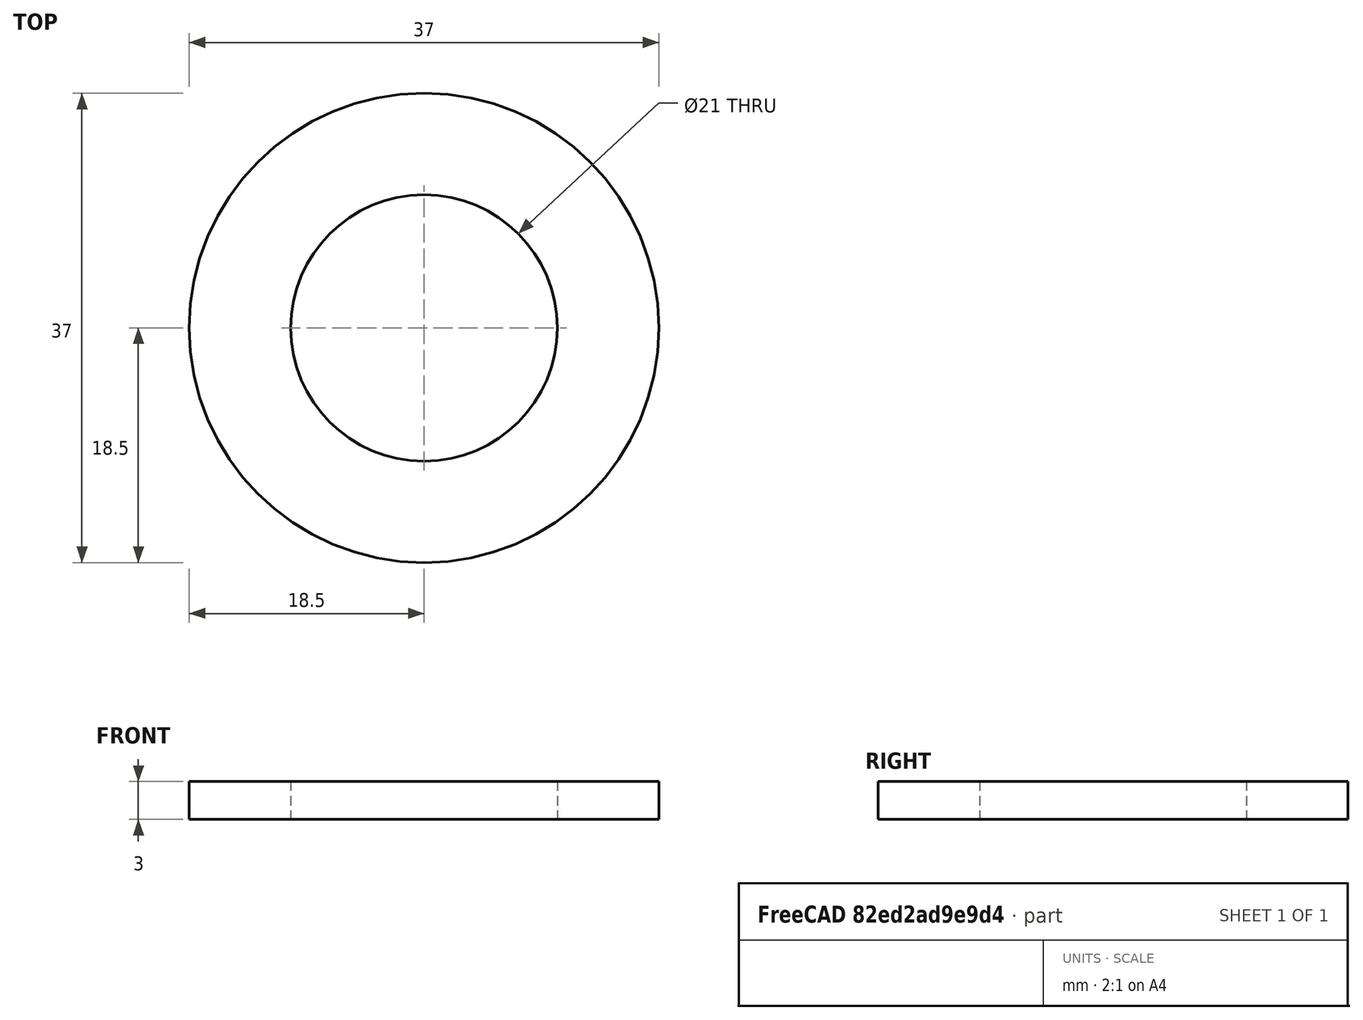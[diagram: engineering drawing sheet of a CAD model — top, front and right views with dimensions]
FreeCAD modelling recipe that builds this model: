
FCSTD DOCUMENT  (FreeCAD 0.14R3700 (Git))
Label: Scheibe DIN 125 - A 21
License: CC-BY 3.0
LicenseURL: http://creativecommons.org/licenses/by/3.0/
objects: Sketcher::SketchObject×1, PartDesign::Revolution×1, Part::Feature×1
note: 4 computed .brp shape members not serialized (recipe doc carries the construction recipe); baked Part::Feature solids carry a one-line shape summary decoded from their .brp

FEATURE [Sketcher::SketchObject] Sketch
  Placement = pos=(0,0,0) rot=(0.57735,0.57735,0.57735;2.0944rad)
  sketch-geometry (4):
    g0: LineSegment StartX=10.5 StartY=0 StartZ=0 EndX=18.5 EndY=0 EndZ=0
    g1: LineSegment StartX=18.5 StartY=0 StartZ=0 EndX=18.5 EndY=3 EndZ=0
    g2: LineSegment StartX=18.5 StartY=3 StartZ=0 EndX=10.5 EndY=3 EndZ=0
    g3: LineSegment StartX=10.5 StartY=3 StartZ=0 EndX=10.5 EndY=0 EndZ=0
  constraints (12):
    c: Coincident(g0,g1)
    c: Coincident(g1,g2)
    c: Coincident(g2,g3)
    c: Coincident(g3,g0)
    c: Horizontal(g0)
    c: Horizontal(g2)
    c: Vertical(g1)
    c: Vertical(g3)
    c: PointOnObject(g0,g-1)
    c: DistanceY(g1) = 3
    c: DistanceX(g-1,g2) = 10.5
    c: DistanceX(g-1,g1) = 18.5
FEATURE [PartDesign::Revolution] Revolution  label="Scheibe DIN 125 - A 21 #"
  Angle = 360
  Axis = (0,0,1)
  Base = (0,0,0)
  Placement = pos=(0,0,0) rot=(0.57735,0.57735,0.57735;2.0944rad)
  ReferenceAxis = -> Sketch [V_Axis]
  Reversed = true
  Sketch = -> Sketch
FEATURE [Part::Feature] Revolution001  label="Scheibe DIN 125 - A 21 #001"
  Placement = pos=(0,0,0) rot=(0.57735,0.57735,0.57735;2.0944rad)
  shape: bbox 37 x 37 x 3 mm, 4 faces (baked)
